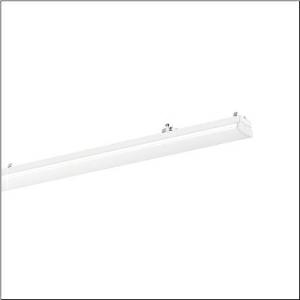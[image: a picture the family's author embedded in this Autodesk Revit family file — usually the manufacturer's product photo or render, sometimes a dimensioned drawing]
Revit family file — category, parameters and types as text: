
# Revit family: licross_r__21_recessed_opal_ho_52tl1dcn4cxm_43b7
name_source: partatom
category: Lighting Fixtures
units: mm (PartAtom-declared; Revit-internal decimal feet)

## family parameters
Cut with Voids When Loaded = No
Host = Face
Light Source = No
Part Type = Normal
Room Calculation Point = No
Round Connector Dimension = Use Diameter
Shared = No

## types (1)
- --- (1 x LED, 12300 lm, 68.4 W, 4000K)
    Apparent Load = 68 VA
    CIE Flux Codes = 44 73 91 87 100
    Color Rendering = 80
    Color Temperature = 4000K
    Default Elevation = 1800 mm
    Description = Licross® 21 recessed opal HO, luminaire insert, of sheet steel, galvanised, coil coated, white, length: 1.500mm, width: 66mm, height: 67mm, LED rated luminous flux: 12.300lm, light colour: 840, control gear: ON/OFF Multilumen, CLOi, with plug, 3-pole, with phase selection, mains connection: 220..240V, AC, 50/60Hz, start of lifetime: 68W, end of service life: 83W, internal wiring halogen-free, primary optical cover: cover, of PMMA, light emission: direct with ceiling illumination distribution, primary light characteristic: symmetric, protection rating (complete): IP40, insulation class (complete): insulation class I (protective earthing), certification: CE, ENEC, VDE, UKCA, protection symbol: D if used in an environment without relevant dust loads with corresponding accessories, impact resistance: IK06, permissible ambient temperature for indoor applications: -35..+30°C, corresponds to IFS (International Featured Standards) requirements for safety and quality in the food industry, reducing of maximum allowable ambient temperature of 5°C with ceiling mounting, LABS conformity tested according to VDMA 24364:2018-05, packaging unit: 1 piece
    Height = 83 mm
    Lamp = 1 x LED
    Lamp Light Flux = 12300 lm
    Lamp Power = 68.4 W
    Lamp count = 1
    Length = 1500 mm
    Luminous efficacy = 180 lm/W
    Manufacturer = Siteco
    ModVariant = No
    Model = 52TL1DCN4CXM
    Mounting Place = Ceiling
    Mounting Type = Pendant
    Number of Poles = 1
    OnlyDefault = Yes
    Power Factor = 1
    Product Name = Licross® 21 recessed opal HO
    Product group = luminaire insert | ceiling pendant
    ProductGroupID = 902
    Protection Class = Protection class I
    Protection Degree = IP 40
    RLX_Detail_Level = 1
    RLX_Emergency_Light_Flux = 0 lm
    RLX_Emergency_Type = 0
    RLX_Emergency_Type_DB = No
    RlxData = <blob elided: 24749 chars, md5=e122391c>
    Socket = socket
    Standby Power = 0 W
    System Light Flux = 12300 lm
    System Power = 68 W
    Type Comments = factory setting: luminous flux: 100 % | (A | C | E) | 161 mA
    Type Image = l_1313666.jpg
    URL = http://relux.com
    VarID = @adj_089661
    Voltage = 0 V
    Weight = 0.00 kg
    Width = 76 mm

## geometry (parser evidence)
native form markers: Blend x4, Sweep x12
no freeform markers — native parametric forms only
